# Revit family: スチール製ベンチフード サイド用W1480xD730xH1600_Shrinkwrap_1
name_source: partatom
category: Generic Models
units: mm (PartAtom-declared; Revit-internal decimal feet)

## family parameters
Always vertical = Yes
Can host rebar = No
Cut with Voids When Loaded = No
Part Type = Normal
Room Calculation Point = No
Round Connector Dimension = Use Diameter
Shared = No
Work Plane-Based = No

## types (1)
- Standard
    Default Elevation = 0 mm  [stored 0 ft]
    Manufacturer = 三進金属工業株式会社
    URL = https://www.sanshinkinzoku.co.jp
    タイプ = サイド実験台用
    品名 = スチールベンチフード
    品番 = HSHD-1500S
    外寸法　奥行-D = 730 mm  [stored 2.39501 ft]
    外寸法　間口-W = 1480 mm  [stored 4.85564 ft]
    外寸法　高さ-H = 1600 mm  [stored 5.24934 ft]
    所用ダクト径（φ） = 250mm
    有効内寸法 高さ-H = 1300 mm  [stored 4.26509 ft]
    有効内寸法　奥行-D = 535 mm  [stored 1.75525 ft]
    有効内寸法　間口-W = 1250 mm  [stored 4.10105 ft]
    本体材質 = スチール（粉体塗装仕上げ）
    本体標準色 = マイルドホワイト
    片面サッシ開口高さ400mm制御風速 = 0.5m/s
    質量 = 220kg
    風量 = 17m3 /min

note: [stored X ft] marks values corroborated as IEEE doubles in the binary element streams (Revit-internal decimal feet)

## geometry (parser evidence)
native form markers: Sweep x3
no freeform markers — native parametric forms only
